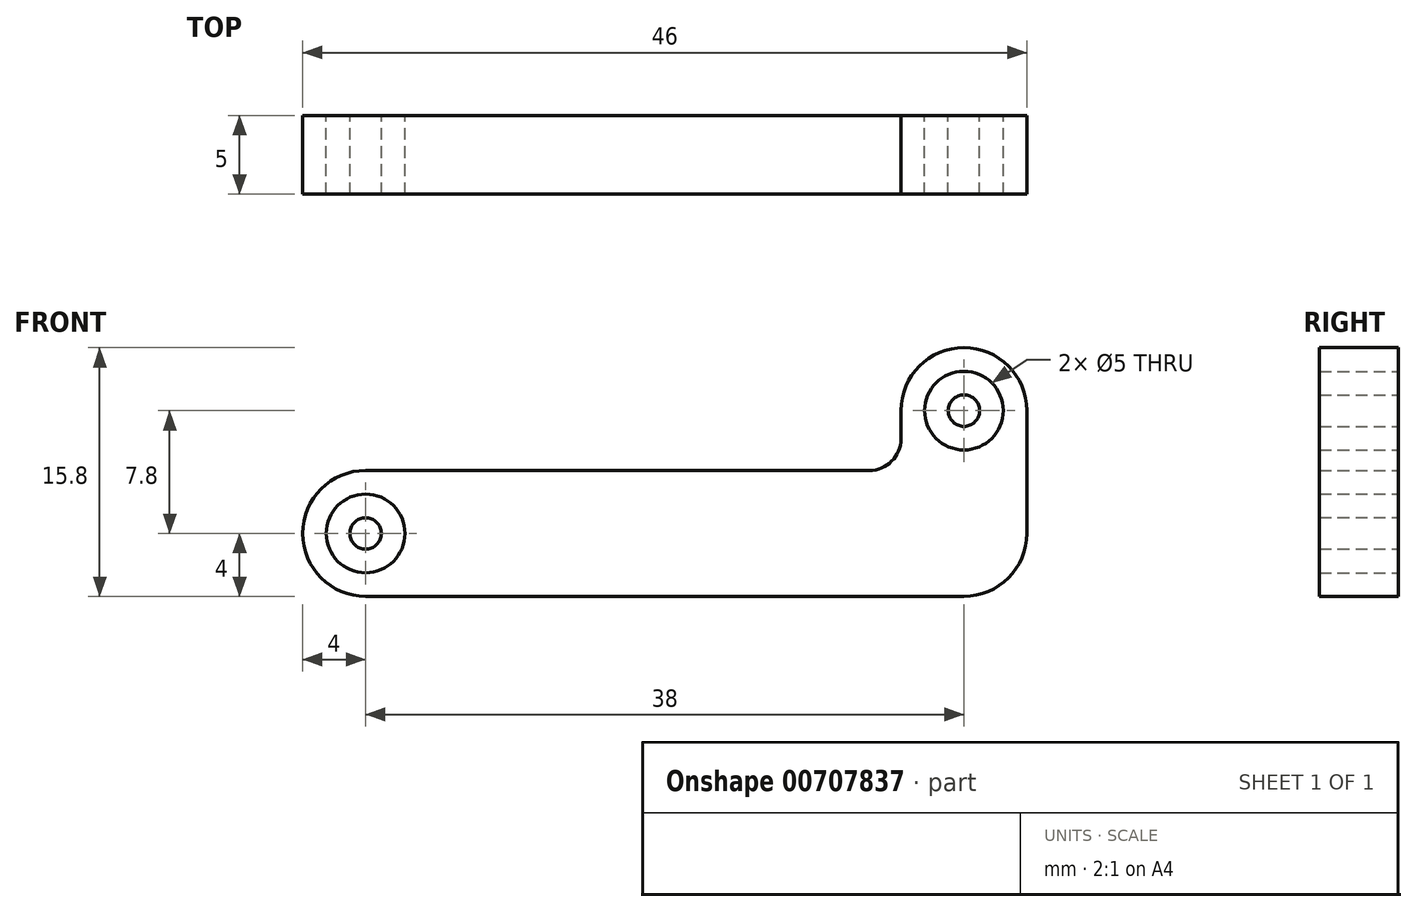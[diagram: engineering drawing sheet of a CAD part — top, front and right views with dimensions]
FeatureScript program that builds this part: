
annotation { "Feature Type Name" : "Feature", "Feature Type Description" : "" }
export const myFeature = defineFeature(function(context is Context, id is Id, definition is map)
    precondition{}
    {
        {
            var Q0;
            Q0=qCreatedBy(makeId("Front.planeOp"),FACE);
            var sketch = newSketch(context, id + "F0", { "sketchPlane" : qUnion([Q0])});
            skLineSegment(sketch, "E0.bottom", {"start": v(0, 0) * mm, "end": v(38, 0) * mm});
            skLineSegment(sketch, "E0.top", {"start": v(0, 8) * mm, "end": v(32, 8) * mm});
            skLineSegment(sketch, "E0.left", {"start": v(0, 0) * mm, "end": v(0, 1.5) * mm});
            skArc(sketch, "E1", {"start": v(0, 8) * mm, "mid": v(-4, 4) * mm, "end": v(0, 0) * mm});
            skArc(sketch, "E2", {"start": v(38, 0) * mm, "mid": v(40.83, 1.17) * mm, "end": v(42, 4) * mm});
            skLineSegment(sketch, "E3", {"start": v(42, 4) * mm, "end": v(42, 11.8) * mm});
            skPoint(sketch, "E3.startSnap0", {"position": v(42, 4) * mm});
            skLineSegment(sketch, "E4", {"start": v(34, 11.8) * mm, "end": v(34, 10) * mm});
            skLineSegment(sketch, "E5", {"start": v(38, 0) * mm, "end": v(34, 0) * mm});
            skPoint(sketch, "E6.orphan", {"position": v(42, 0) * mm});
            skArc(sketch, "E7.trimOffspring", {"start": v(42, 11.8) * mm, "mid": v(38, 15.8) * mm, "end": v(34, 11.8) * mm});
            skPoint(sketch, "E8.trimOffspring.end.orphan", {"position": v(38, 8) * mm});
            skPoint(sketch, "E9.visualSharp", {"position": v(34, 8) * mm});
            skArc(sketch, "E9.filletArc", {"start": v(32, 8) * mm, "mid": v(33.41, 8.59) * mm, "end": v(34, 10) * mm});
            skCircle(sketch, "E10", {"center": v(0, 4) * mm, "radius": 2.5 * mm});
            skCircle(sketch, "E11", {"center": v(0, 4) * mm, "radius": 1 * mm});
            skCircle(sketch, "E12", {"center": v(38, 11.8) * mm, "radius": 2.5 * mm});
            skCircle(sketch, "E13", {"center": v(38, 11.8) * mm, "radius": 1 * mm});
            skSolve(sketch);
        }
        {
            var Q0;
            Q0=makeQuery(id+"F0.imprint","IMPRINT",FACE,{"disambiguationData":[TD([[makeQuery(id+"F0.imprint","IMPRINT",EDGE,{"derivedFrom":sQuery(id+"F0.wireOp",EDGE,"E0.bottom")}),1.0]])]});
            var Q1;
            Q1=makeQuery(id+"F0.imprint","IMPRINT",FACE,{"disambiguationData":[TD([[makeQuery(id+"F0.imprint","IMPRINT",EDGE,{"derivedFrom":sQuery(id+"F0.wireOp",EDGE,"E11")}),1.0]])]});
            var Q2;
            Q2=makeQuery(id+"F0.imprint","IMPRINT",FACE,{"disambiguationData":[TD([[makeQuery(id+"F0.imprint","IMPRINT",EDGE,{"derivedFrom":sQuery(id+"F0.wireOp",EDGE,"E13")}),1.0]])]});
            extrude(context, id + "F1", {"entities" : qUnion([Q0, Q1, Q2]), "depth" : 5 * mm, "offsetDistance" : 25.4 * mm});
        }
    });
